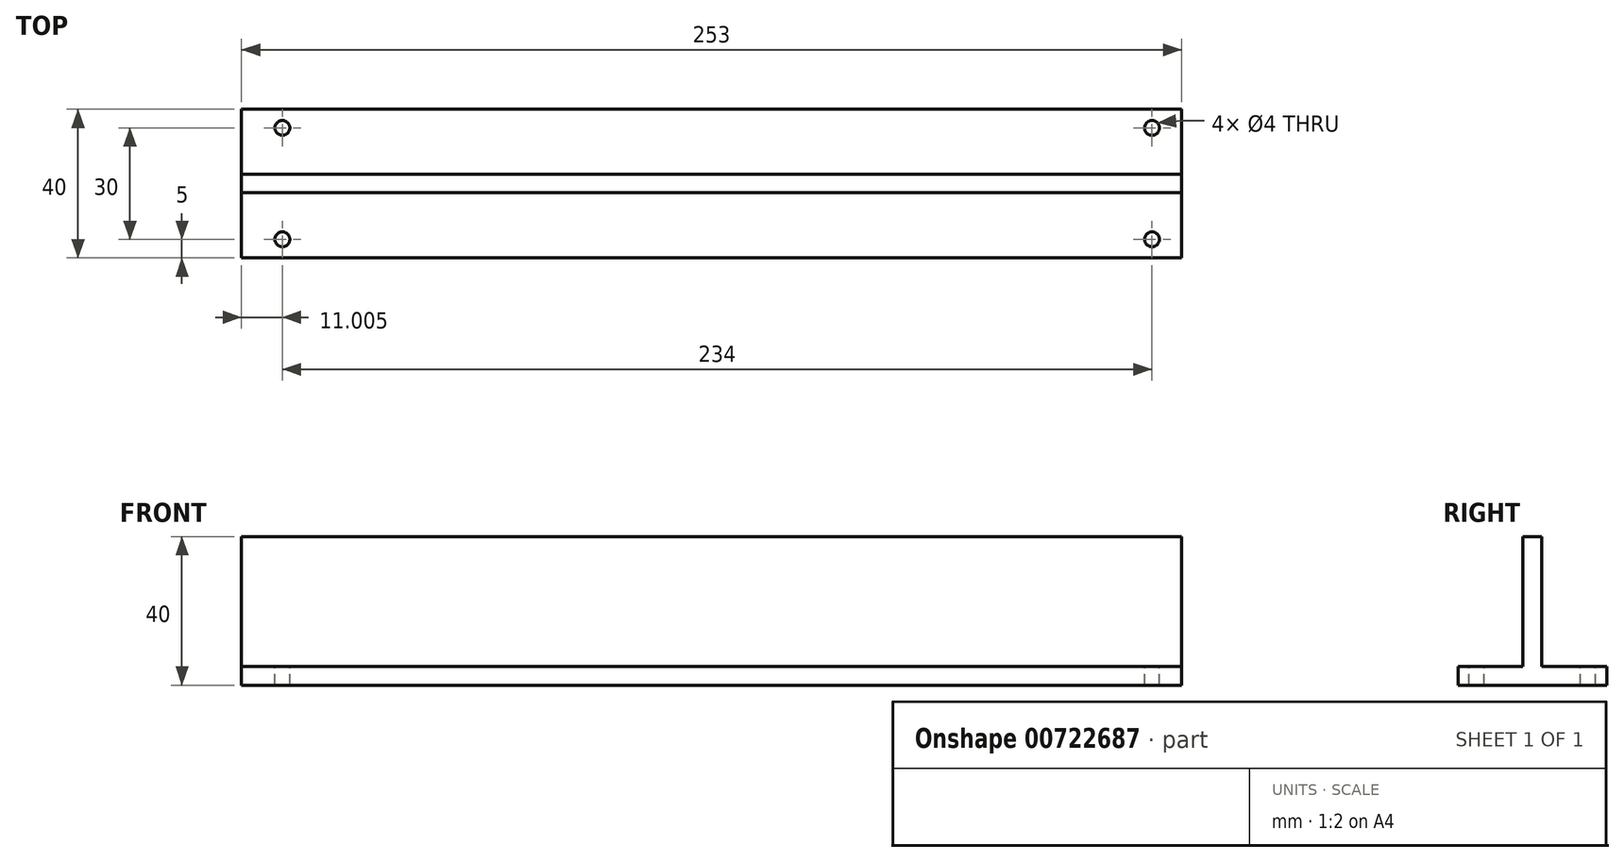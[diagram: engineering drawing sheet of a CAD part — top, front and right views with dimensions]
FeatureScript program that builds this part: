
annotation { "Feature Type Name" : "Feature", "Feature Type Description" : "" }
export const myFeature = defineFeature(function(context is Context, id is Id, definition is map)
    precondition{}
    {
        {
            var Q0;
            Q0=qCreatedBy(makeId("Top.planeOp"),FACE);
            var sketch = newSketch(context, id + "F0", { "sketchPlane" : qUnion([Q0])});
            skLineSegment(sketch, "E0.bottom", {"start": v(-125.98, -35) * mm, "end": v(127.02, -35) * mm});
            skLineSegment(sketch, "E0.top", {"start": v(-125.98, 5) * mm, "end": v(127.02, 5) * mm});
            skLineSegment(sketch, "E0.left", {"start": v(-125.98, -35) * mm, "end": v(-125.98, 5) * mm});
            skLineSegment(sketch, "E0.right", {"start": v(127.02, -35) * mm, "end": v(127.02, 5) * mm});
            skPoint(sketch, "E1", {"position": v(-114.98, 0) * mm});
            skPoint(sketch, "E2", {"position": v(-114.98, -30) * mm});
            skPoint(sketch, "E3", {"position": v(119.02, -30) * mm});
            skPoint(sketch, "E4", {"position": v(119.02, 0) * mm});
            skLineSegment(sketch, "E5", {"start": v(-136.45, -15) * mm, "end": v(148.28, -15) * mm, "construction": true});
            skPoint(sketch, "E5.startSnap0", {"position": v(-125.98, -15) * mm});
            skLineSegment(sketch, "E6", {"start": v(-125.98, -17.5) * mm, "end": v(127.02, -17.5) * mm});
            skLineSegment(sketch, "E7", {"start": v(127.02, -17.5) * mm, "end": v(127.02, -12.5) * mm});
            skLineSegment(sketch, "E8", {"start": v(127.02, -12.5) * mm, "end": v(-125.98, -12.5) * mm});
            skLineSegment(sketch, "E9", {"start": v(-125.98, -12.5) * mm, "end": v(-125.98, -17.5) * mm});
            skSolve(sketch);
        }
        {
            var Q0;
            Q0=makeQuery(id+"F0.imprint","IMPRINT",FACE,{"disambiguationData":[TD([[makeQuery(id+"F0.imprint","IMPRINT",EDGE,{"derivedFrom":sQuery(id+"F0.wireOp",EDGE,"E0.bottom")}),1.0]])]});
            extrude(context, id + "F1", {"entities" : qUnion([Q0]), "depth" : 5 * mm, "offsetDistance" : 25 * mm});
        }
        {
            var Q0;
            Q0=sQuery(id+"F0.wireOp",VERTEX,"E1");
            var Q1;
            Q1=sQuery(id+"F0.wireOp",VERTEX,"E2");
            var Q2;
            Q2=sQuery(id+"F0.wireOp",VERTEX,"E3");
            var Q3;
            Q3=sQuery(id+"F0.wireOp",VERTEX,"E4");
            var Q4;
            Q4=makeQuery(id+"F1.opExtrude","SWEPT_BODY",BODY,{"disambiguationData":[OSD([sQuery(id+"F0.wireOp",EDGE,"E0.bottom"),sQuery(id+"F0.wireOp",EDGE,"E0.top"),sQuery(id+"F0.wireOp",EDGE,"E0.left"),sQuery(id+"F0.wireOp",EDGE,"E0.right")])]});
            hole(context, id + "F2", {"style" : HoleStyle.SIMPLE, "endStyle" : HoleEndStyle.THROUGH, "oppositeDirection" : true, "holeDiameter" : 4 * mm, "majorDiameter" : 5 * mm, "isTappedThrough" : true, "tappedDepth" : 12 * mm, "tapClearance" : 3, "locations" : qUnion([Q0, Q1, Q2, Q3]), "scope" : qUnion([Q4])});
        }
        {
            var Q0;
            Q0=makeQuery(id+"F0.imprint","IMPRINT",FACE,{"disambiguationData":[TD([[makeQuery(id+"F0.imprint","IMPRINT",EDGE,{"derivedFrom":sQuery(id+"F0.wireOp",EDGE,"E6")}),1.0]])]});
            extrude(context, id + "F3", {"entities" : qUnion([Q0]), "operationType" : NewBodyOperationType.ADD, "depth" : 40 * mm, "offsetDistance" : 25 * mm});
        }
        {
            var Q0;
            {var subQ0=sQuery(id+"F0.wireOp",EDGE,"E0.top");Q0=makeQuery(id+"F0.imprint","IMPRINT",FACE,{"disambiguationData":[TD([[makeQuery(id+"F0.imprint","IMPRINT",EDGE,{"derivedFrom":subQ0}),-1.0]])]});}
            extrude(context, id + "F4", {"entities" : qUnion([Q0]), "operationType" : NewBodyOperationType.ADD, "depth" : 5 * mm, "offsetDistance" : 25 * mm});
        }
        {
            var Q0;
            Q0=sQuery(id+"F0.wireOp",VERTEX,"E1");
            var Q1;
            Q1=sQuery(id+"F0.wireOp",VERTEX,"E4");
            var Q2;
            Q2=makeQuery(id+"F1.opExtrude","SWEPT_BODY",BODY,{"disambiguationData":[OSD([sQuery(id+"F0.wireOp",EDGE,"E0.bottom"),sQuery(id+"F0.wireOp",EDGE,"E0.left"),sQuery(id+"F0.wireOp",EDGE,"E0.right"),sQuery(id+"F0.wireOp",EDGE,"E6")])]});
            hole(context, id + "F5", {"style" : HoleStyle.SIMPLE, "endStyle" : HoleEndStyle.THROUGH, "oppositeDirection" : true, "holeDiameter" : 4 * mm, "majorDiameter" : 5 * mm, "isTappedThrough" : true, "tappedDepth" : 12 * mm, "tapClearance" : 3, "locations" : qUnion([Q0, Q1]), "scope" : qUnion([Q2])});
        }
    });
